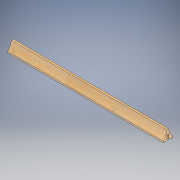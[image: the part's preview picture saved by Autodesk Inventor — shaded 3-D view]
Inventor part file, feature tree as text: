
AUTODESK INVENTOR PART (.ipt)
format: ipt  version: 2022.2 (Build 262287010, 287A)  size: 189,952 bytes
history: native  units: in
note: dims shown in document units (in); Inventor stores cm internally (conversion verified against a paired STEP export)
features: revolve x2, direct_edit x1, extrude x1, sketch x1, projected_geometry x1, other x1
ambient origin geometry x8: Origin, YZ Plane, XZ Plane, XY Plane, X Axis, Y Axis, Z Axis, Center Point
bodies: Solid1 (feature_tree)
feature tree (7):
  direct_edit  "Direct Edit1"
  extrude  "Extrusion1"  TaperAngle=180.0deg  [1 undecoded]
  sketch  "Sketch1"  dims[d0=-0.6184in d1=180.0deg d2=0.0625in d3=0.0in]
  projected_geometry  "Projected Loop1"
  other  "Mull (lower)"
  revolve  "Rotate1"  [1 undecoded]
  revolve  "Rotate2"  [1 undecoded]
note: 3 required parameter values undecoded (feature->parameter linkage not recoverable at this tier; creation-order binding heuristic only, values carry confidence <= 0.55)